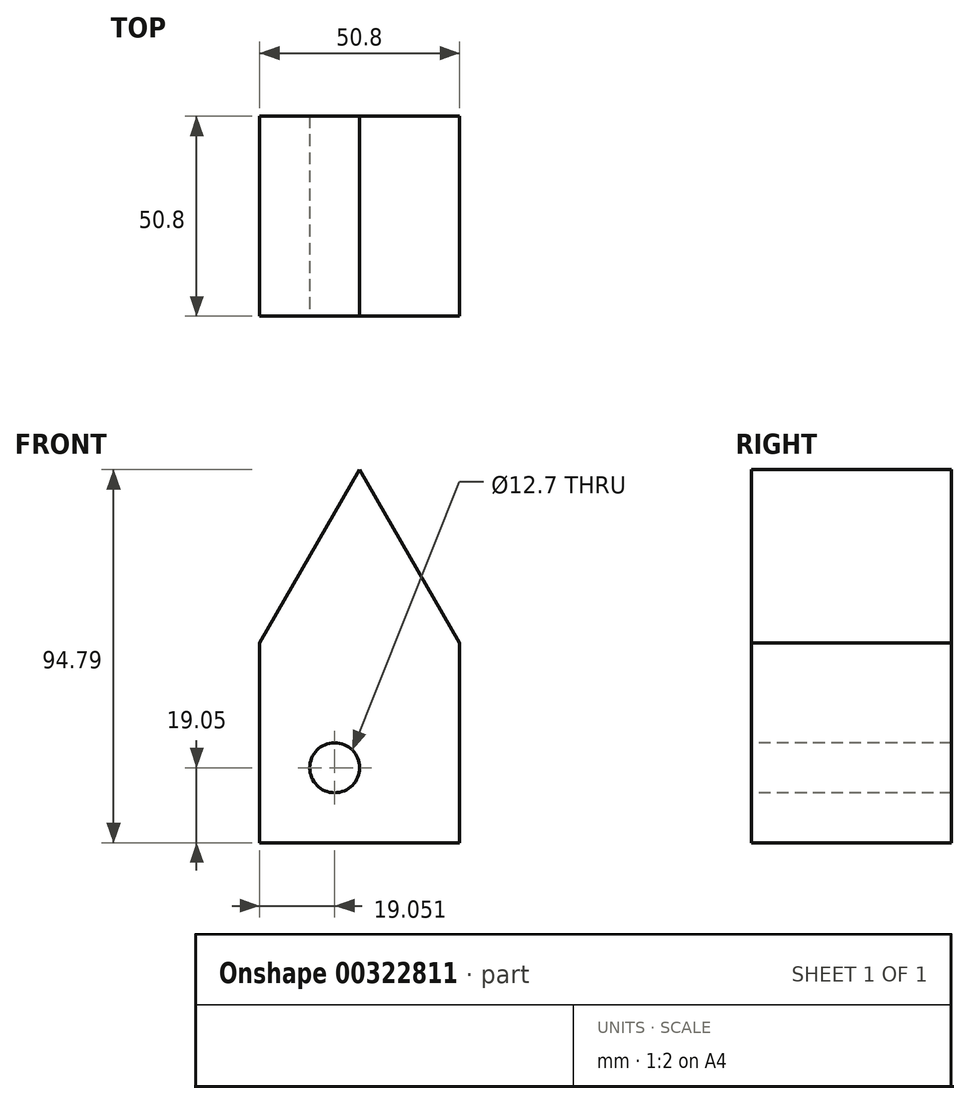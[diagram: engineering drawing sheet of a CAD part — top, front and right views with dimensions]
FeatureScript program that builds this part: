
annotation { "Feature Type Name" : "Feature", "Feature Type Description" : "" }
export const myFeature = defineFeature(function(context is Context, id is Id, definition is map)
    precondition{}
    {
        {
            var Q0;
            Q0=qCreatedBy(makeId("Front.planeOp"),FACE);
            var sketch = newSketch(context, id + "F0", { "sketchPlane" : qUnion([Q0])});
            skLineSegment(sketch, "E0.top", {"start": v(-9.45, 0) * mm, "end": v(41.35, 0) * mm});
            skLineSegment(sketch, "E0.left", {"start": v(-9.45, 50.8) * mm, "end": v(-9.45, 0) * mm});
            skLineSegment(sketch, "E0.right", {"start": v(41.35, 50.8) * mm, "end": v(41.35, 0) * mm});
            skLineSegment(sketch, "E1", {"start": v(-9.45, 50.8) * mm, "end": v(15.95, 94.8) * mm});
            skLineSegment(sketch, "E2", {"start": v(15.95, 94.8) * mm, "end": v(41.35, 50.8) * mm});
            skCircle(sketch, "E3", {"center": v(9.6, 19.05) * mm, "radius": 6.35 * mm});
            skSolve(sketch);
        }
        {
            var Q0;
            Q0=makeQuery(id+"F0.imprint","IMPRINT",FACE,{"disambiguationData":[TD([[makeQuery(id+"F0.imprint","IMPRINT",EDGE,{"derivedFrom":sQuery(id+"F0.wireOp",EDGE,"E0.left")}),1.0]])]});
            extrude(context, id + "F1", {"entities" : qUnion([Q0]), "oppositeDirection" : true, "depth" : 50.8 * mm});
        }
    });
